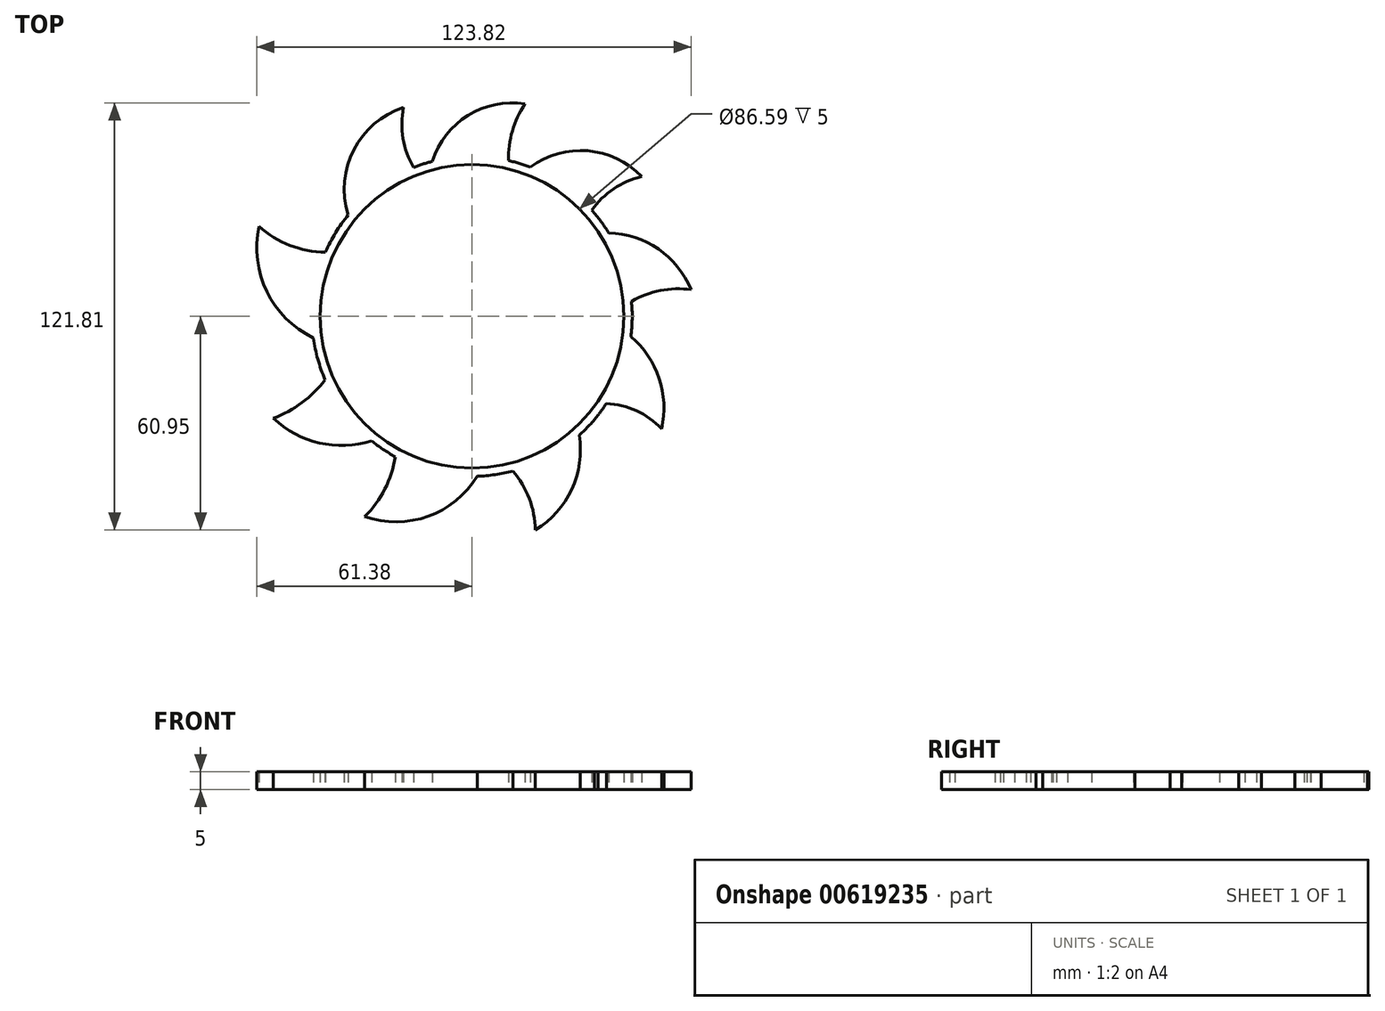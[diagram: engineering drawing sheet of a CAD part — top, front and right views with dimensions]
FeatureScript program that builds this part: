
annotation { "Feature Type Name" : "Feature", "Feature Type Description" : "" }
export const myFeature = defineFeature(function(context is Context, id is Id, definition is map)
    precondition{}
    {
        {
            var Q0;
            Q0=qCreatedBy(makeId("Top.planeOp"),FACE);
            var sketch = newSketch(context, id + "F0", { "sketchPlane" : qUnion([Q0])});
            skCircle(sketch, "E0", {"center": v(0, 0) * mm, "radius": 43.3 * mm});
            skArc(sketch, "E1", {"start": v(35.92, -28.15) * mm, "mid": v(-35.38, 28.83) * mm, "end": v(34.82, -29.5) * mm});
            skCircle(sketch, "E2.cCircle", {"center": v(0, 0) * mm, "radius": 38.29 * mm, "construction": true});
            skLineSegment(sketch, "E2.0", {"start": v(-38.76, -0.67) * mm, "end": v(-37.07, 11.34) * mm, "construction": true});
            skLineSegment(sketch, "E2.1", {"start": v(-37.07, 11.34) * mm, "end": v(-31.75, 22.24) * mm, "construction": true});
            skLineSegment(sketch, "E2.2", {"start": v(-31.75, 22.24) * mm, "end": v(-23.33, 30.96) * mm, "construction": true});
            skLineSegment(sketch, "E2.3", {"start": v(-23.33, 30.96) * mm, "end": v(-12.62, 36.66) * mm, "construction": true});
            skLineSegment(sketch, "E2.4", {"start": v(-12.62, 36.66) * mm, "end": v(-0.67, 38.76) * mm, "construction": true});
            skLineSegment(sketch, "E2.5", {"start": v(-0.67, 38.76) * mm, "end": v(11.34, 37.07) * mm, "construction": true});
            skLineSegment(sketch, "E2.6", {"start": v(11.34, 37.07) * mm, "end": v(22.24, 31.75) * mm, "construction": true});
            skLineSegment(sketch, "E2.7", {"start": v(22.24, 31.75) * mm, "end": v(30.96, 23.33) * mm, "construction": true});
            skLineSegment(sketch, "E2.8", {"start": v(30.96, 23.33) * mm, "end": v(36.66, 12.62) * mm, "construction": true});
            skLineSegment(sketch, "E2.9", {"start": v(36.66, 12.62) * mm, "end": v(38.76, 0.67) * mm, "construction": true});
            skLineSegment(sketch, "E2.10", {"start": v(38.76, 0.67) * mm, "end": v(37.07, -11.34) * mm, "construction": true});
            skLineSegment(sketch, "E2.11", {"start": v(37.07, -11.34) * mm, "end": v(31.75, -22.24) * mm, "construction": true});
            skLineSegment(sketch, "E2.12", {"start": v(31.75, -22.24) * mm, "end": v(23.33, -30.96) * mm, "construction": true});
            skLineSegment(sketch, "E2.13", {"start": v(23.33, -30.96) * mm, "end": v(12.62, -36.66) * mm, "construction": true});
            skLineSegment(sketch, "E2.14", {"start": v(12.62, -36.66) * mm, "end": v(0.67, -38.76) * mm, "construction": true});
            skLineSegment(sketch, "E2.15", {"start": v(0.67, -38.76) * mm, "end": v(-11.34, -37.07) * mm, "construction": true});
            skLineSegment(sketch, "E2.16", {"start": v(-11.34, -37.07) * mm, "end": v(-22.24, -31.75) * mm, "construction": true});
            skLineSegment(sketch, "E2.17", {"start": v(-22.24, -31.75) * mm, "end": v(-30.96, -23.33) * mm, "construction": true});
            skLineSegment(sketch, "E2.18", {"start": v(-30.96, -23.33) * mm, "end": v(-36.66, -12.62) * mm, "construction": true});
            skLineSegment(sketch, "E2.19", {"start": v(-36.66, -12.62) * mm, "end": v(-38.76, -0.67) * mm, "construction": true});
            skPoint(sketch, "E2.0.midPoint", {"position": v(-37.92, 5.33) * mm});
            skArc(sketch, "E3.trimOffspring", {"start": v(11.1, 36.65) * mm, "mid": v(11.1, 36.88) * mm, "end": v(11.09, 37.1) * mm});
            skArc(sketch, "E4.trimOffspring", {"start": v(30.75, 22.82) * mm, "mid": v(30.95, 22.9) * mm, "end": v(31.15, 22.98) * mm});
            skArc(sketch, "E5.trimOffspring", {"start": v(-12.46, 37) * mm, "mid": v(-12.45, 37) * mm, "end": v(-12.45, 37) * mm});
            skArc(sketch, "E6.trimOffspring", {"start": v(-31.58, 22.42) * mm, "mid": v(-31.44, 22.24) * mm, "end": v(-31.3, 22.05) * mm});
            skArc(sketch, "E7.trimOffspring", {"start": v(37.07, -9.58) * mm, "mid": v(37.19, -9.64) * mm, "end": v(37.3, -9.7) * mm});
            skArc(sketch, "E8.trimOffspring", {"start": v(30.57, 23.06) * mm, "mid": v(30.7, 23.25) * mm, "end": v(30.84, 23.45) * mm});
            skArc(sketch, "E9.trimOffspring", {"start": v(11.1, 37.1) * mm, "mid": v(11.08, 36.88) * mm, "end": v(11.06, 36.66) * mm});
            skArc(sketch, "E10", {"start": v(-19.54, 59.56) * mm, "mid": v(-33.73, 47.5) * mm, "end": v(-35.28, 28.94) * mm});
            skArc(sketch, "E11", {"start": v(-19.54, 59.56) * mm, "mid": v(-19.7, 50.75) * mm, "end": v(-16.68, 42.48) * mm});
            skArc(sketch, "E12.trimOffspring", {"start": v(12.35, 36.24) * mm, "mid": v(12.35, 36.4) * mm, "end": v(12.35, 36.58) * mm});
            skArc(sketch, "E13.trimOffspring", {"start": v(-15.36, 40.48) * mm, "mid": v(-13.62, 38.37) * mm, "end": v(-11.65, 36.48) * mm});
            skArc(sketch, "E14.trimOffspring", {"start": v(-34.32, 26.4) * mm, "mid": v(-33.06, 23.97) * mm, "end": v(-31.55, 21.7) * mm});
            skArc(sketch, "E15", {"start": v(15.09, 60.56) * mm, "mid": v(-1.18, 57.3) * mm, "end": v(-11.36, 44.2) * mm});
            skArc(sketch, "E16", {"start": v(15.09, 60.56) * mm, "mid": v(11.48, 52.87) * mm, "end": v(10.39, 44.44) * mm});
            skArc(sketch, "E17.trimOffspring", {"start": v(30.56, 23.06) * mm, "mid": v(30.7, 23.26) * mm, "end": v(30.84, 23.45) * mm});
            skArc(sketch, "E18", {"start": v(48.3, 39.86) * mm, "mid": v(32.96, 47.2) * mm, "end": v(16.6, 42.5) * mm});
            skArc(sketch, "E19", {"start": v(48.3, 39.86) * mm, "mid": v(40.34, 36.37) * mm, "end": v(34.13, 30.3) * mm});
            skArc(sketch, "E20.trimOffspring", {"start": v(38.23, -2.14) * mm, "mid": v(38.3, -2.2) * mm, "end": v(38.35, -2.24) * mm});
            skArc(sketch, "E21.trimOffspring", {"start": v(38.29, 0.52) * mm, "mid": v(38.52, 0.6) * mm, "end": v(38.76, 0.67) * mm});
            skArc(sketch, "E22", {"start": v(62.44, 7.59) * mm, "mid": v(53.11, 19.18) * mm, "end": v(38.96, 23.76) * mm});
            skArc(sketch, "E23", {"start": v(62.44, 7.59) * mm, "mid": v(53.66, 7.36) * mm, "end": v(45.44, 4.27) * mm});
            skArc(sketch, "E24.trimOffspring", {"start": v(32.46, -20.31) * mm, "mid": v(32.47, -20.52) * mm, "end": v(32.5, -20.73) * mm});
            skArc(sketch, "E25.trimOffspring", {"start": v(28, -26.11) * mm, "mid": v(28, -26.11) * mm, "end": v(28.01, -26.11) * mm});
            skArc(sketch, "E26.trimOffspring", {"start": v(43.2, 2.8) * mm, "mid": v(40.57, 0.6) * mm, "end": v(38.24, -1.91) * mm});
            skArc(sketch, "E27", {"start": v(54, -32.08) * mm, "mid": v(53.32, -17.7) * mm, "end": v(45.27, -5.78) * mm});
            skArc(sketch, "E28", {"start": v(54, -32.08) * mm, "mid": v(46.84, -26.93) * mm, "end": v(38.25, -24.89) * mm});
            skArc(sketch, "E29.trimOffspring", {"start": v(4.17, -38.06) * mm, "mid": v(4.19, -38.1) * mm, "end": v(4.2, -38.14) * mm});
            skArc(sketch, "E30.trimOffspring", {"start": v(35.38, -24.95) * mm, "mid": v(31.78, -25.56) * mm, "end": v(28.31, -26.73) * mm});
            skArc(sketch, "E31.trimOffspring", {"start": v(43.1, -4.13) * mm, "mid": v(40.75, -2.69) * mm, "end": v(38.26, -1.5) * mm});
            skArc(sketch, "E32.trimOffspring", {"start": v(36.25, 23.68) * mm, "mid": v(33.53, 23.32) * mm, "end": v(30.86, 22.67) * mm});
            skFitSpline(sketch, "E33", {"points": [v(35.92, -28.15) * mm, v(34.82, -29.5) * mm], "startDerivative": vector(-1.1, -1.35) * mm, "endDerivative": vector(-1.1, -1.35) * mm});
            skArc(sketch, "E34.trimOffspring", {"start": v(20.4, -32.4) * mm, "mid": v(20.3, -32.51) * mm, "end": v(20.2, -32.62) * mm});
            skArc(sketch, "E35", {"start": v(-21.65, -31.58) * mm, "mid": v(-21.7, -31.79) * mm, "end": v(-21.75, -32) * mm});
            skArc(sketch, "E36", {"start": v(9.8, -42.17) * mm, "mid": v(7.13, -39.93) * mm, "end": v(4.2, -38.06) * mm});
            skArc(sketch, "E37.trimOffspring", {"start": v(26.63, -27.54) * mm, "mid": v(26.6, -27.56) * mm, "end": v(26.56, -27.58) * mm});
            skArc(sketch, "E38.trimOffspring", {"start": v(-14.59, -35.4) * mm, "mid": v(-14.64, -35.42) * mm, "end": v(-14.7, -35.43) * mm});
            skArc(sketch, "E39.trimOffspring", {"start": v(29.97, -31.25) * mm, "mid": v(29.12, -28.63) * mm, "end": v(28, -26.1) * mm});
            skArc(sketch, "E40.trimOffspring", {"start": v(18.03, -60.95) * mm, "mid": v(28.41, -49.34) * mm, "end": v(30.54, -33.91) * mm});
            skArc(sketch, "E41.trimOffspring", {"start": v(18.03, -60.95) * mm, "mid": v(16.3, -51.98) * mm, "end": v(11.64, -44.13) * mm});
            skArc(sketch, "E42", {"start": v(-36.63, -9.08) * mm, "mid": v(-36.92, -9.28) * mm, "end": v(-37.2, -9.48) * mm});
            skArc(sketch, "E43", {"start": v(-30.6, -57.1) * mm, "mid": v(-24.87, -49.27) * mm, "end": v(-21.89, -40.04) * mm});
            skArc(sketch, "E44.trimOffspring", {"start": v(-36.63, -9.08) * mm, "mid": v(-36.99, -8.87) * mm, "end": v(-37.35, -8.67) * mm});
            skArc(sketch, "E45.trimOffspring", {"start": v(-30.6, -57.1) * mm, "mid": v(-12.53, -57.04) * mm, "end": v(1.46, -45.61) * mm});
            skArc(sketch, "E46.trimOffspring", {"start": v(-21.6, -37.52) * mm, "mid": v(-21.55, -34.5) * mm, "end": v(-21.79, -31.49) * mm});
            skArc(sketch, "E47.trimOffspring", {"start": v(2.76, -43.2) * mm, "mid": v(3.82, -40.66) * mm, "end": v(4.61, -38.01) * mm});
            skArc(sketch, "E48", {"start": v(-32.95, 19.5) * mm, "mid": v(-33.02, 19.5) * mm, "end": v(-33.08, 19.52) * mm});
            skArc(sketch, "E49", {"start": v(-56.65, -29.11) * mm, "mid": v(-48.5, -24.63) * mm, "end": v(-41.9, -18.08) * mm});
            skArc(sketch, "E50.trimOffspring", {"start": v(-56.65, -29.11) * mm, "mid": v(-43.54, -36.11) * mm, "end": v(-28.68, -35.5) * mm});
            skArc(sketch, "E51.trimOffspring", {"start": v(-36.47, 11.67) * mm, "mid": v(-36.55, 11.95) * mm, "end": v(-36.64, 12.22) * mm});
            skArc(sketch, "E52.trimOffspring", {"start": v(-40.31, -15.8) * mm, "mid": v(-38.55, -12.65) * mm, "end": v(-37.13, -9.35) * mm});
            skArc(sketch, "E53.trimOffspring", {"start": v(-26.1, -34.54) * mm, "mid": v(-23.6, -33.33) * mm, "end": v(-21.23, -31.87) * mm});
            skArc(sketch, "E54.trimOffspring", {"start": v(32.82, 28.24) * mm, "mid": v(31.56, 25.68) * mm, "end": v(30.62, 23) * mm});
            skArc(sketch, "E55.trimOffspring", {"start": v(14.55, 40.78) * mm, "mid": v(12.68, 38.82) * mm, "end": v(11.05, 36.66) * mm});
            skArc(sketch, "E56.trimOffspring", {"start": v(10.56, 41.99) * mm, "mid": v(11.04, 39.17) * mm, "end": v(11.8, 36.42) * mm});
            skArc(sketch, "E57", {"start": v(-60.7, 25.65) * mm, "mid": v(-51.94, 20.22) * mm, "end": v(-41.8, 18.3) * mm});
            skArc(sketch, "E58.trimOffspring", {"start": v(-60.7, 25.65) * mm, "mid": v(-58.5, 7.05) * mm, "end": v(-45.22, -6.14) * mm});
            skArc(sketch, "E59.trimOffspring", {"start": v(-14.06, 40.73) * mm, "mid": v(-14.03, 40.85) * mm, "end": v(-14, 40.97) * mm});
            skArc(sketch, "E60.trimOffspring", {"start": v(-14.06, 40.73) * mm, "mid": v(-14.15, 40.8) * mm, "end": v(-14.24, 40.89) * mm});
            skArc(sketch, "E61.trimOffspring", {"start": v(-39.19, 18.4) * mm, "mid": v(-35.96, 18.88) * mm, "end": v(-32.82, 19.73) * mm});
            skArc(sketch, "E62.trimOffspring", {"start": v(-42.7, -7.2) * mm, "mid": v(-40.04, -8.03) * mm, "end": v(-37.31, -8.59) * mm});
            skFitSpline(sketch, "E63", {"points": [v(-11.18, 41) * mm, v(-11.65, 36.48) * mm], "startDerivative": vector(-0.46, -4.52) * mm, "endDerivative": vector(-0.46, -4.52) * mm});
            skSolve(sketch);
        }
        {
            var Q0;
            Q0 = qSketchRegion(id + "F0", true);
            extrude(context, id + "F1", {"entities" : qUnion([Q0]), "depth" : 5 * mm, "offsetDistance" : 25 * mm});
        }
    });
